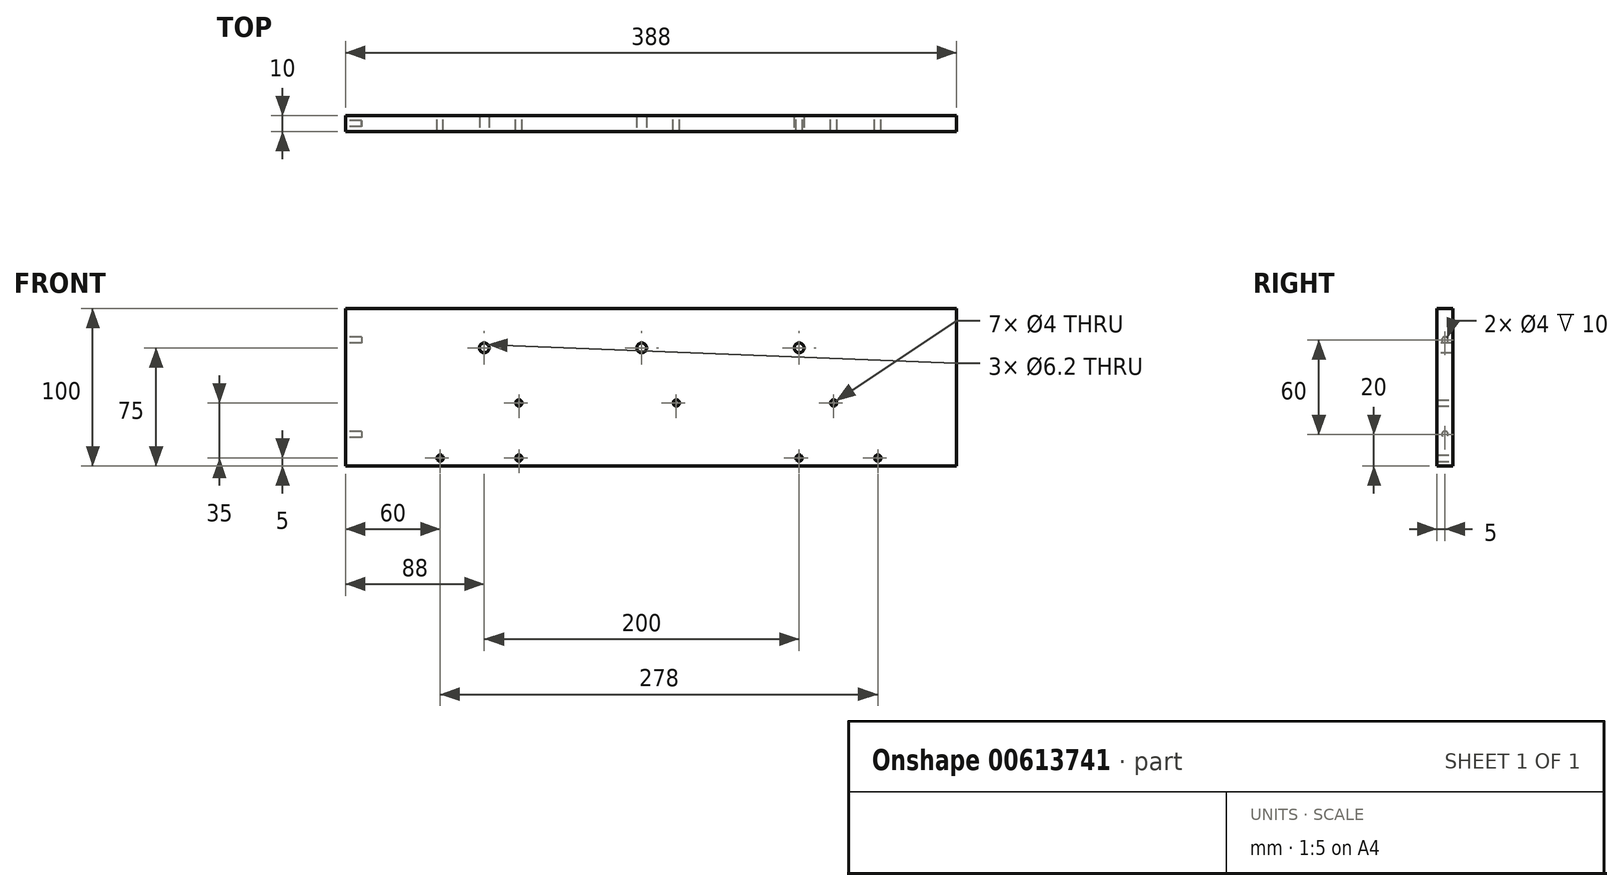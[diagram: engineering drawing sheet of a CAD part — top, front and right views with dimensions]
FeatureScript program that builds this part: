
annotation { "Feature Type Name" : "Feature", "Feature Type Description" : "" }
export const myFeature = defineFeature(function(context is Context, id is Id, definition is map)
    precondition{}
    {
        {
            var Q0;
            Q0=qCreatedBy(makeId("Front.planeOp"),FACE);
            var sketch = newSketch(context, id + "F0", { "sketchPlane" : qUnion([Q0])});
            skLineSegment(sketch, "E0.bottom", {"start": v(194, 50) * mm, "end": v(-194, 50) * mm});
            skLineSegment(sketch, "E0.top", {"start": v(194, -50) * mm, "end": v(-194, -50) * mm});
            skLineSegment(sketch, "E0.left", {"start": v(194, 50) * mm, "end": v(194, -50) * mm});
            skLineSegment(sketch, "E0.right", {"start": v(-194, 50) * mm, "end": v(-194, -50) * mm});
            skPoint(sketch, "E0.middle", {"position": v(0, 0) * mm});
            skCircle(sketch, "E1", {"center": v(144, -45) * mm, "radius": 2 * mm});
            skCircle(sketch, "E2", {"center": v(-134, -45) * mm, "radius": 2 * mm});
            skPoint(sketch, "E3", {"position": v(0, -45) * mm});
            skCircle(sketch, "E4", {"center": v(116, -10) * mm, "radius": 2 * mm});
            skCircle(sketch, "E5", {"center": v(16, -10) * mm, "radius": 2 * mm});
            skCircle(sketch, "E6", {"center": v(-84, -10) * mm, "radius": 2 * mm});
            skLineSegment(sketch, "E7", {"start": v(-84, -10) * mm, "end": v(16, -10) * mm, "construction": true});
            skLineSegment(sketch, "E8", {"start": v(116, -10) * mm, "end": v(16, -10) * mm, "construction": true});
            skCircle(sketch, "E9", {"center": v(-84, -45) * mm, "radius": 2 * mm});
            skCircle(sketch, "E10", {"center": v(94, -45) * mm, "radius": 2 * mm});
            skSolve(sketch);
        }
        {
            var Q0;
            Q0=qSketchRegion(id+"F0",true);
            extrude(context, id + "F1", {"entities" : qUnion([Q0]), "depth" : 10 * mm, "offsetDistance" : 25 * mm});
        }
        {
            var Q0;
            Q0=makeQuery(id+"F1.opExtrude","CAP_FACE",FACE,{"disambiguationData":[OSD([sQuery(id+"F0.wireOp",EDGE,"E0.bottom"),sQuery(id+"F0.wireOp",EDGE,"E0.top"),sQuery(id+"F0.wireOp",EDGE,"E0.left"),sQuery(id+"F0.wireOp",EDGE,"E0.right"),sQuery(id+"F0.wireOp",EDGE,"E1"),sQuery(id+"F0.wireOp",EDGE,"E2"),sQuery(id+"F0.wireOp",EDGE,"E4"),sQuery(id+"F0.wireOp",EDGE,"E5"),sQuery(id+"F0.wireOp",EDGE,"E6")])],"isStart":false});
            var sketch = newSketch(context, id + "F2", { "sketchPlane" : qUnion([Q0])});
            skCircle(sketch, "E11", {"center": v(-6, 25) * mm, "radius": 3.1 * mm});
            skCircle(sketch, "E12", {"center": v(94, 25) * mm, "radius": 3.1 * mm});
            skCircle(sketch, "E13", {"center": v(-106, 25) * mm, "radius": 3.1 * mm});
            skSolve(sketch);
        }
        {
            var Q0;
            Q0=qSketchRegion(id+"F2",true);
            extrude(context, id + "F3", {"entities" : qUnion([Q0]), "operationType" : NewBodyOperationType.REMOVE, "oppositeDirection" : true, "depth" : 10 * mm, "offsetDistance" : 25 * mm});
        }
        {
            var Q0;
            Q0=makeQuery(id+"F1.opExtrude","SWEPT_FACE",FACE,{"disambiguationData":[OSD([sQuery(id+"F0.wireOp",EDGE,"E0.right")])]});
            var sketch = newSketch(context, id + "F4", { "sketchPlane" : qUnion([Q0])});
            skCircle(sketch, "E14", {"center": v(5, -30) * mm, "radius": 2 * mm});
            skCircle(sketch, "E15", {"center": v(5, 30) * mm, "radius": 2 * mm});
            skPoint(sketch, "E15.centerSnap0", {"position": v(5, 50) * mm});
            skSolve(sketch);
        }
        {
            var Q0;
            Q0=qSketchRegion(id+"F4",true);
            extrude(context, id + "F5", {"entities" : qUnion([Q0]), "operationType" : NewBodyOperationType.REMOVE, "oppositeDirection" : true, "depth" : 10 * mm, "offsetDistance" : 25 * mm});
        }
    });
